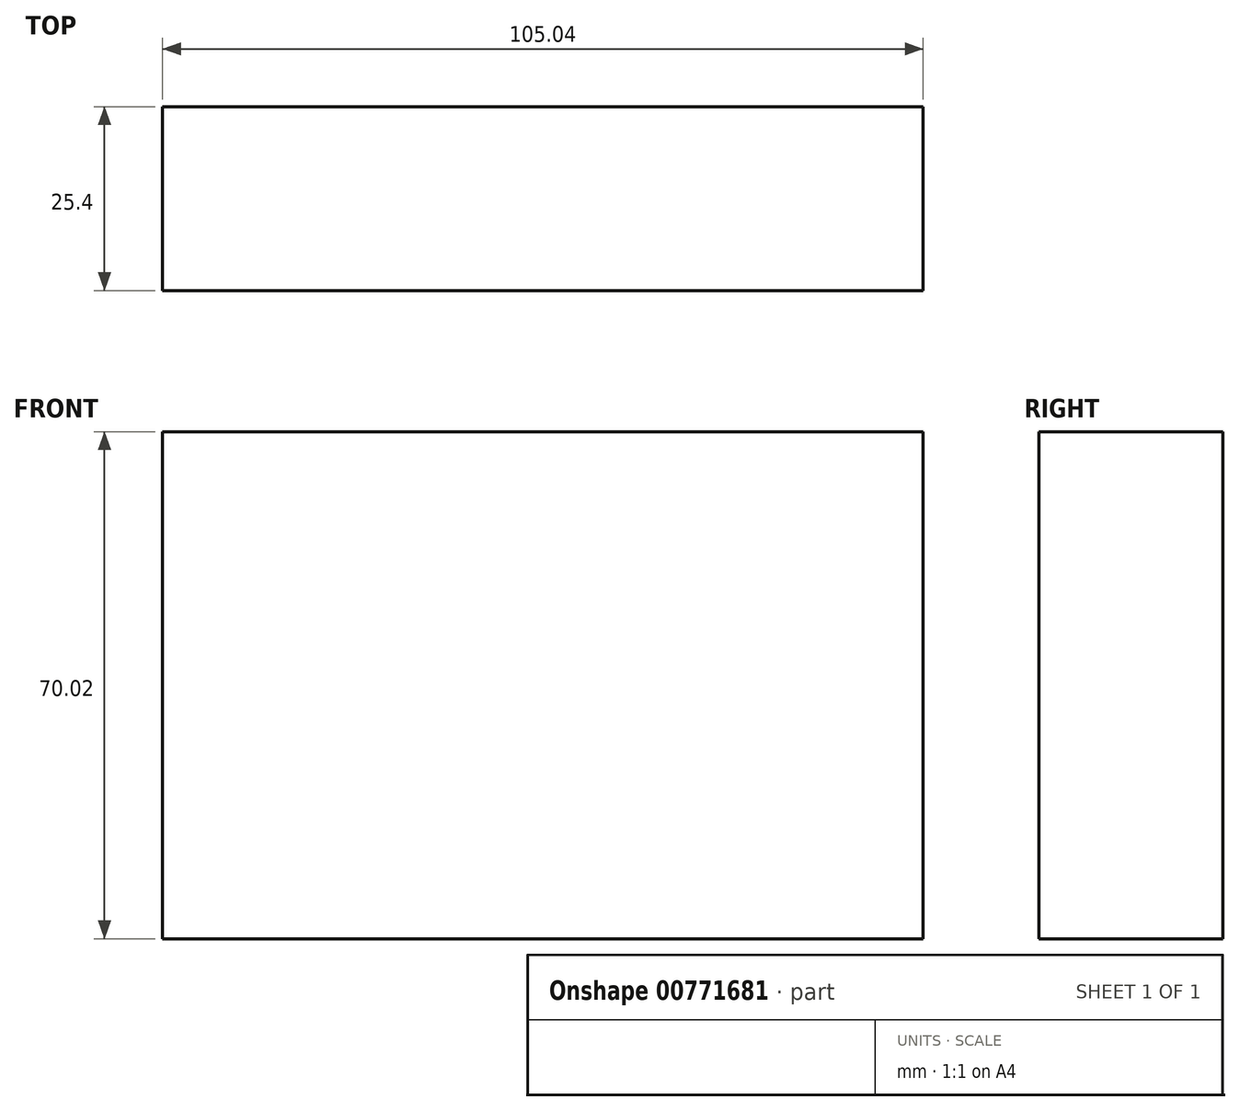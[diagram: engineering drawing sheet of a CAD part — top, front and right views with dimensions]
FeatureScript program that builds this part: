
annotation { "Feature Type Name" : "Feature", "Feature Type Description" : "" }
export const myFeature = defineFeature(function(context is Context, id is Id, definition is map)
    precondition{}
    {
        {
            var Q0;
            Q0=qCreatedBy(makeId("Front.planeOp"),FACE);
            var sketch = newSketch(context, id + "F0", { "sketchPlane" : qUnion([Q0])});
            skLineSegment(sketch, "E0.bottom", {"start": v(-52.52, -35.01) * mm, "end": v(52.52, -35.01) * mm});
            skLineSegment(sketch, "E0.top", {"start": v(-52.52, 35.01) * mm, "end": v(52.52, 35.01) * mm});
            skLineSegment(sketch, "E0.left", {"start": v(-52.52, -35.01) * mm, "end": v(-52.52, 35.01) * mm});
            skLineSegment(sketch, "E0.right", {"start": v(52.52, -35.01) * mm, "end": v(52.52, 35.01) * mm});
            skPoint(sketch, "E0.middle", {"position": v(0, 0) * mm});
            skSolve(sketch);
        }
        {
            var Q0;
            Q0=makeQuery(id+"F0.imprint","IMPRINT",FACE,{"disambiguationData":[TD([[makeQuery(id+"F0.imprint","IMPRINT",EDGE,{"derivedFrom":sQuery(id+"F0.wireOp",EDGE,"E0.bottom")}),1.0]])]});
            extrude(context, id + "F1", {"entities" : qUnion([Q0]), "depth" : 25.4 * mm, "offsetDistance" : 25.4 * mm});
        }
    });
